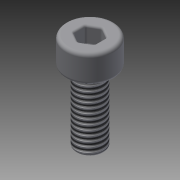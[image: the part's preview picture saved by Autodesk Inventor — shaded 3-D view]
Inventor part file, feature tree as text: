
AUTODESK INVENTOR PART (.ipt)
format: ipt  version: 2013 (Build 170138000, 138)  size: 162,304 bytes
history: native  units: mm
features: extrude x3, sketch x3, fillet x2, other x1, thread x1
ambient origin geometry x1: Origin
feature tree (10):
  other  "ソリッド1"
  extrude  "押し出し1"  Depth=7.0mm
  extrude  "押し出し2"  Depth=4.0mm TaperAngle=0.0deg
  extrude  "押し出し3"  Depth=4.0mm
  thread  "ねじ1"
  fillet  "フィレット1"  Radius=10.0mm
  fillet  "フィレット2"  Radius=1.5mm
  sketch  "スケッチ1"
  sketch  "スケッチ2"
  sketch  "スケッチ3"
